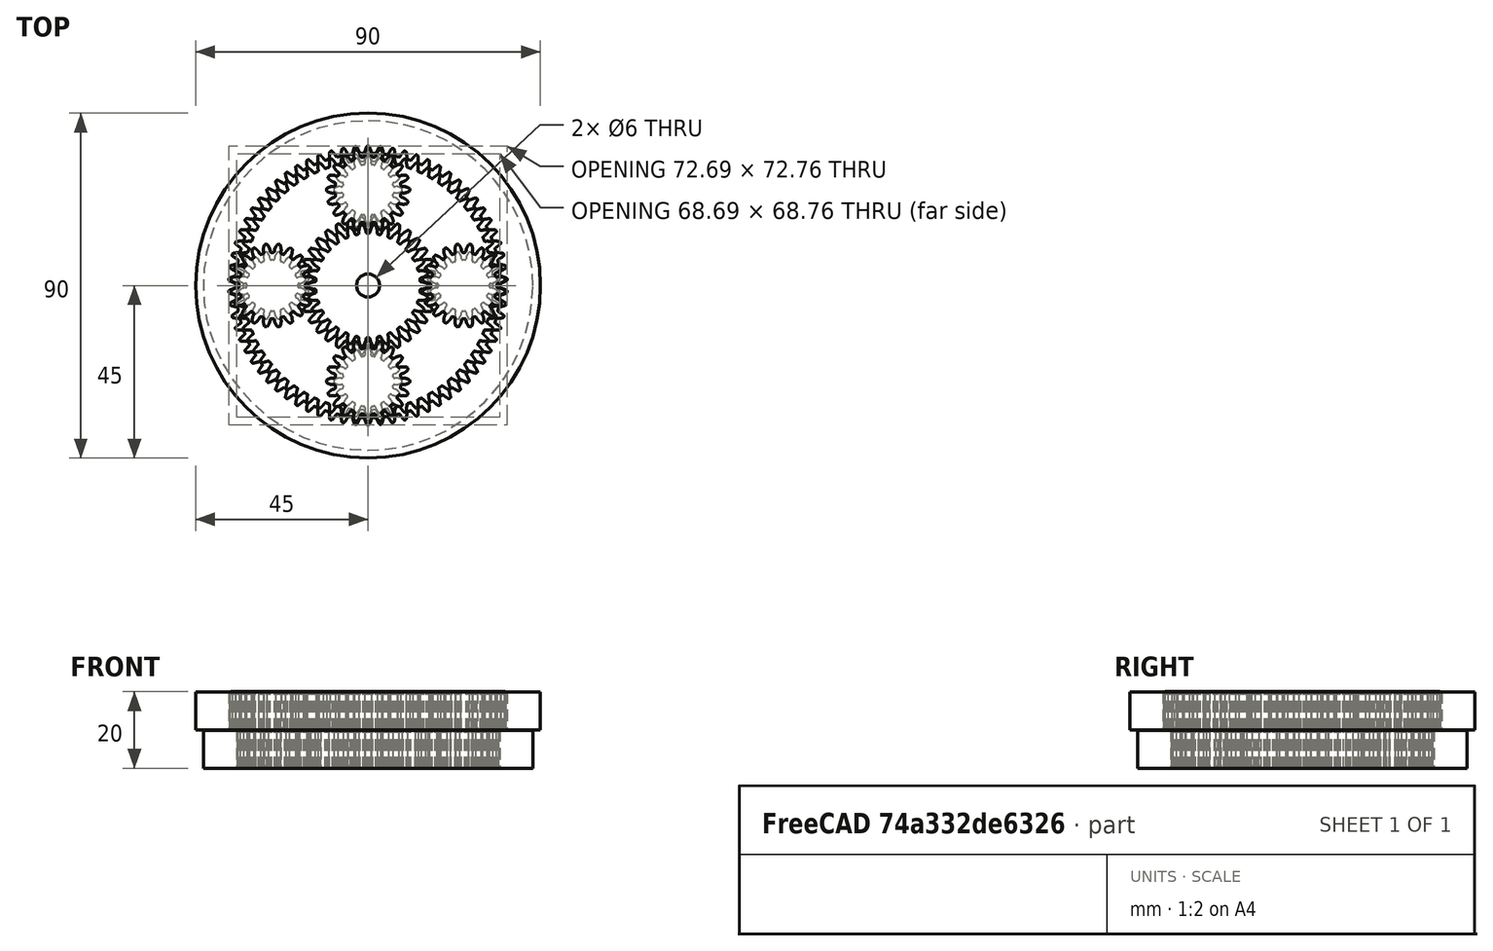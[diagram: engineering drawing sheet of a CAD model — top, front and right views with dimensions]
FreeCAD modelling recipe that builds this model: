
FCSTD DOCUMENT  (FreeCAD 0.18R15380 (Git))
Label: compound_planetary
License: All rights reserved
LicenseURL: http://en.wikipedia.org/wiki/All_rights_reserved
objects: Part::Part2DObjectPython×12, Part::Extrusion×12, Part::Cylinder×4, Part::Cut×4
note: 32 computed .brp shape members not serialized (recipe doc carries the construction recipe); baked Part::Feature solids carry a one-line shape summary decoded from their .brp

FEATURE [Part::Part2DObjectPython] first_sun_involute  # Draft 2D object (typed FeaturePython)
  ExternalGear = true
  HighPrecision = true
  Modules = 0.992647
  NumberOfTeeth = 34
  PressureAngle = 20
FEATURE [Part::Extrusion] first_sun_trimmed
  Base = -> first_sun_involute
  Dir = (0,0,1)
  DirMode = 2
  FaceMakerClass = Part::FaceMakerBullseye
  LengthFwd = 10
  LengthRev = 0
  Solid = true
  Symmetric = false
FEATURE [Part::Cylinder] first_sun_bore
  Angle = 360
  AttacherType = Attacher::AttachEngine3D
  Height = 10.1
  Radius = 3
FEATURE [Part::Cut] first_sun
  Base = -> first_sun_trimmed
  Tool = -> first_sun_bore
FEATURE [Part::Part2DObjectPython] first_planet_0_involute  # Draft 2D object (typed FeaturePython)
  ExternalGear = true
  HighPrecision = true
  Modules = 0.984375
  NumberOfTeeth = 16
  PressureAngle = 20
FEATURE [Part::Extrusion] first_planet_0
  Base = -> first_planet_0_involute
  Dir = (0,0,1)
  DirMode = 2
  FaceMakerClass = Part::FaceMakerBullseye
  LengthFwd = 10
  LengthRev = 0
  Placement = pos=(25,0,0) rot=(0,0,1;0.19635rad)
  Solid = true
  Symmetric = false
FEATURE [Part::Part2DObjectPython] first_planet_1_involute  # Draft 2D object (typed FeaturePython)
  ExternalGear = true
  HighPrecision = true
  Modules = 0.984375
  NumberOfTeeth = 16
  PressureAngle = 20
FEATURE [Part::Extrusion] first_planet_1
  Base = -> first_planet_1_involute
  Dir = (0,0,1)
  DirMode = 2
  FaceMakerClass = Part::FaceMakerBullseye
  LengthFwd = 10
  LengthRev = 0
  Placement = pos=(1.5e-15,25,0) rot=(0,0,1;-4.71239rad)
  Solid = true
  Symmetric = false
FEATURE [Part::Part2DObjectPython] first_planet_2_involute  # Draft 2D object (typed FeaturePython)
  ExternalGear = true
  HighPrecision = true
  Modules = 0.984375
  NumberOfTeeth = 16
  PressureAngle = 20
FEATURE [Part::Extrusion] first_planet_2
  Base = -> first_planet_2_involute
  Dir = (0,0,1)
  DirMode = 2
  FaceMakerClass = Part::FaceMakerBullseye
  LengthFwd = 10
  LengthRev = 0
  Placement = pos=(-25,3.1e-15,0) rot=(0,0,1;-9.62113rad)
  Solid = true
  Symmetric = false
FEATURE [Part::Part2DObjectPython] first_planet_3_involute  # Draft 2D object (typed FeaturePython)
  ExternalGear = true
  HighPrecision = true
  Modules = 0.984375
  NumberOfTeeth = 16
  PressureAngle = 20
FEATURE [Part::Extrusion] first_planet_3
  Base = -> first_planet_3_involute
  Dir = (0,0,1)
  DirMode = 2
  FaceMakerClass = Part::FaceMakerBullseye
  LengthFwd = 10
  LengthRev = 0
  Placement = pos=(-4.6e-15,-25,0) rot=(0,0,1;-14.5299rad)
  Solid = true
  Symmetric = false
FEATURE [Part::Part2DObjectPython] first_ring_involute  # Draft 2D object (typed FeaturePython)
  ExternalGear = false
  HighPrecision = true
  Modules = 1.00379
  NumberOfTeeth = 66
  PressureAngle = 20
FEATURE [Part::Extrusion] first_ring_ext
  Base = -> first_ring_involute
  Dir = (0,0,1)
  DirMode = 2
  FaceMakerClass = Part::FaceMakerBullseye
  LengthFwd = 10
  LengthRev = 0
  Solid = true
  Symmetric = false
FEATURE [Part::Cylinder] first_ring_trimmed  label="first_ring_exthousing"
  Angle = 360
  AttacherType = Attacher::AttachEngine3D
  Height = 9.9
  Radius = 43
FEATURE [Part::Cut] first_ring
  Base = -> first_ring_trimmed
  Placement = pos=(0,0,0) rot=(0,0,1;0.0952rad)
  Tool = -> first_ring_ext
FEATURE [Part::Part2DObjectPython] second_sun_involute  # Draft 2D object (typed FeaturePython)
  ExternalGear = true
  HighPrecision = true
  Modules = 0.991667
  NumberOfTeeth = 30
  PressureAngle = 20
FEATURE [Part::Extrusion] second_sun_trimmed
  Base = -> second_sun_involute
  Dir = (0,0,1)
  DirMode = 2
  FaceMakerClass = Part::FaceMakerBullseye
  LengthFwd = 10
  LengthRev = 0
  Solid = true
  Symmetric = false
FEATURE [Part::Cylinder] second_sun_bore
  Angle = 360
  AttacherType = Attacher::AttachEngine3D
  Height = 10.1
  Radius = 3
FEATURE [Part::Cut] second_sun
  Base = -> second_sun_trimmed
  Placement = pos=(0,0,10) rot=(0,0,1;0rad)
  Tool = -> second_sun_bore
FEATURE [Part::Part2DObjectPython] second_planet_0_involute  # Draft 2D object (typed FeaturePython)
  ExternalGear = true
  HighPrecision = true
  Modules = 0.9875
  NumberOfTeeth = 20
  PressureAngle = 20
FEATURE [Part::Extrusion] second_planet_0
  Base = -> second_planet_0_involute
  Dir = (0,0,1)
  DirMode = 2
  FaceMakerClass = Part::FaceMakerBullseye
  LengthFwd = 10
  LengthRev = 0
  Placement = pos=(25,0,10) rot=(0,0,1;0.15708rad)
  Solid = true
  Symmetric = false
FEATURE [Part::Part2DObjectPython] second_planet_1_involute  # Draft 2D object (typed FeaturePython)
  ExternalGear = true
  HighPrecision = true
  Modules = 0.9875
  NumberOfTeeth = 20
  PressureAngle = 20
FEATURE [Part::Extrusion] second_planet_1
  Base = -> second_planet_1_involute
  Dir = (0,0,1)
  DirMode = 2
  FaceMakerClass = Part::FaceMakerBullseye
  LengthFwd = 10
  LengthRev = 0
  Placement = pos=(1.5e-15,25,10) rot=(0,0,1;-3.76991rad)
  Solid = true
  Symmetric = false
FEATURE [Part::Part2DObjectPython] second_planet_2_involute  # Draft 2D object (typed FeaturePython)
  ExternalGear = true
  HighPrecision = true
  Modules = 0.9875
  NumberOfTeeth = 20
  PressureAngle = 20
FEATURE [Part::Extrusion] second_planet_2
  Base = -> second_planet_2_involute
  Dir = (0,0,1)
  DirMode = 2
  FaceMakerClass = Part::FaceMakerBullseye
  LengthFwd = 10
  LengthRev = 0
  Placement = pos=(-25,3.1e-15,10) rot=(0,0,1;-7.6969rad)
  Solid = true
  Symmetric = false
FEATURE [Part::Part2DObjectPython] second_planet_3_involute  # Draft 2D object (typed FeaturePython)
  ExternalGear = true
  HighPrecision = true
  Modules = 0.9875
  NumberOfTeeth = 20
  PressureAngle = 20
FEATURE [Part::Extrusion] second_planet_3
  Base = -> second_planet_3_involute
  Dir = (0,0,1)
  DirMode = 2
  FaceMakerClass = Part::FaceMakerBullseye
  LengthFwd = 10
  LengthRev = 0
  Placement = pos=(-4.6e-15,-25,10) rot=(0,0,1;-11.6239rad)
  Solid = true
  Symmetric = false
FEATURE [Part::Part2DObjectPython] second_ring_involute  # Draft 2D object (typed FeaturePython)
  ExternalGear = false
  HighPrecision = true
  Modules = 1.00357
  NumberOfTeeth = 70
  PressureAngle = 20
FEATURE [Part::Extrusion] second_ring_ext
  Base = -> second_ring_involute
  Dir = (0,0,1)
  DirMode = 2
  FaceMakerClass = Part::FaceMakerBullseye
  LengthFwd = 10
  LengthRev = 0
  Solid = true
  Symmetric = false
FEATURE [Part::Cylinder] second_ring_trimmed  label="second_ring_exthousing"
  Angle = 360
  AttacherType = Attacher::AttachEngine3D
  Height = 9.9
  Radius = 45
FEATURE [Part::Cut] second_ring
  Base = -> second_ring_trimmed
  Placement = pos=(0,0,10) rot=(0,0,1;0.08976rad)
  Tool = -> second_ring_ext
